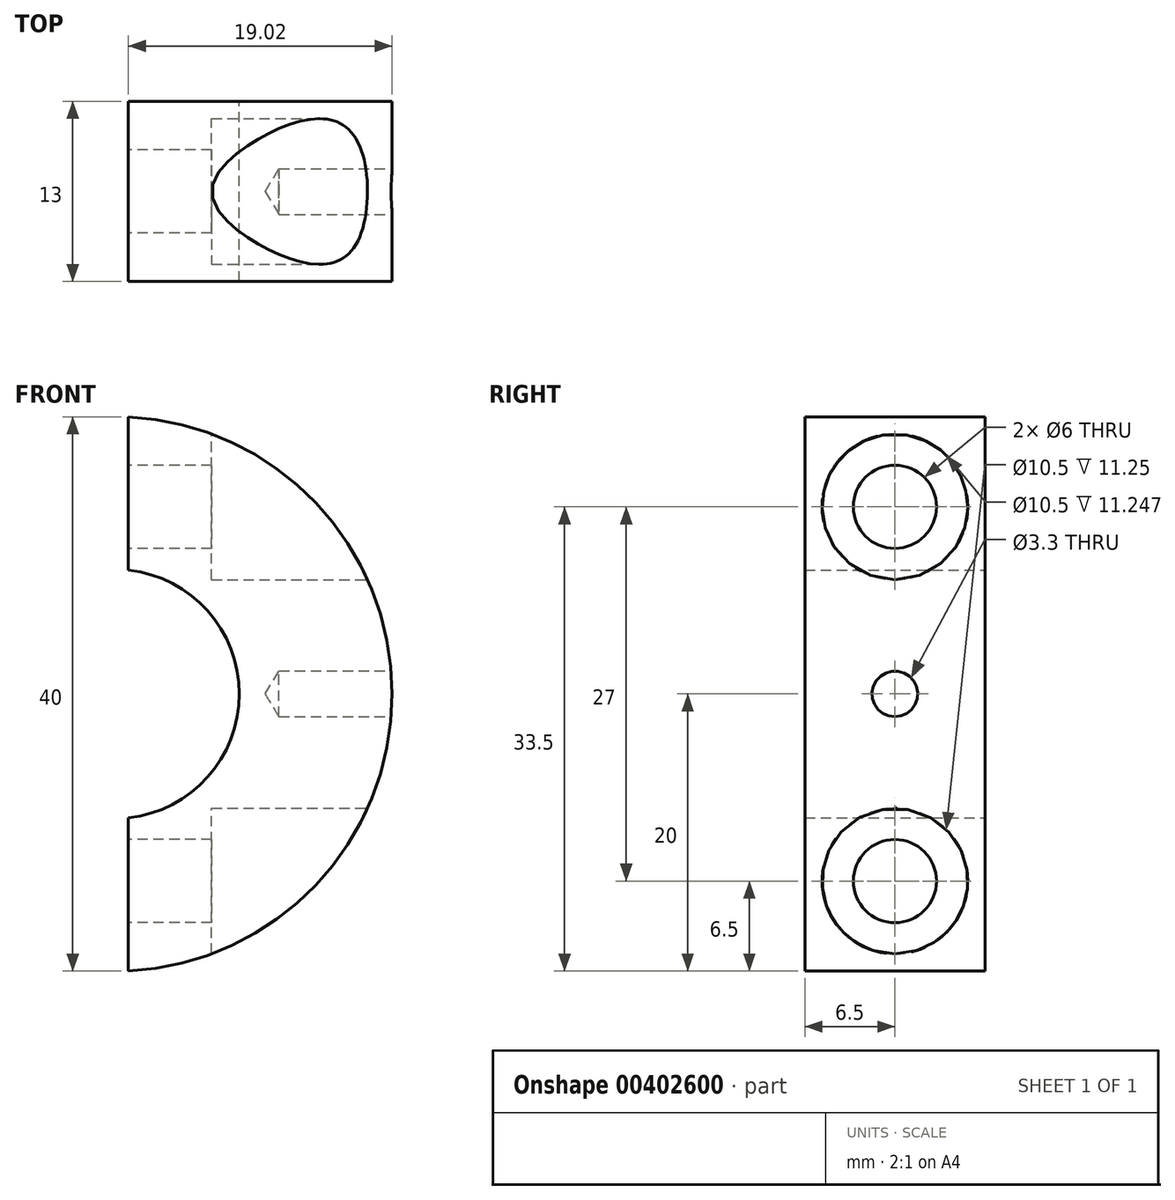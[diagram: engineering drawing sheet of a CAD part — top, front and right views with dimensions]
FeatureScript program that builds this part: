
annotation { "Feature Type Name" : "Feature", "Feature Type Description" : "" }
export const myFeature = defineFeature(function(context is Context, id is Id, definition is map)
    precondition{}
    {
        {
            var Q0;
            Q0=qCreatedBy(makeId("Front.planeOp"),FACE);
            var sketch = newSketch(context, id + "F0", { "sketchPlane" : qUnion([Q0])});
            skLineSegment(sketch, "E0", {"start": v(0, 0) * mm, "end": v(1, 0) * mm, "construction": true});
            skArc(sketch, "E1", {"start": v(1, -8.94) * mm, "mid": v(9, 0) * mm, "end": v(1, 8.94) * mm});
            skLineSegment(sketch, "E2", {"start": v(1, 0) * mm, "end": v(1, -8.94) * mm, "construction": true});
            skLineSegment(sketch, "E3", {"start": v(1, 0) * mm, "end": v(1, 8.94) * mm, "construction": true});
            skLineSegment(sketch, "E4", {"start": v(1, 8.94) * mm, "end": v(1, 20) * mm});
            skLineSegment(sketch, "E5", {"start": v(1, -8.94) * mm, "end": v(1, -20) * mm});
            skLineSegment(sketch, "E6", {"start": v(1, 13.5) * mm, "end": v(22.49, 13.5) * mm, "construction": true});
            skLineSegment(sketch, "E7", {"start": v(1, 16.5) * mm, "end": v(22.49, 16.5) * mm, "construction": true});
            skLineSegment(sketch, "E8", {"start": v(1, 10.5) * mm, "end": v(22.49, 10.5) * mm, "construction": true});
            skLineSegment(sketch, "E9", {"start": v(22.49, 16.5) * mm, "end": v(22.49, 13.5) * mm, "construction": true});
            skLineSegment(sketch, "E10", {"start": v(22.49, 13.5) * mm, "end": v(22.49, 10.5) * mm, "construction": true});
            skArc(sketch, "E11", {"start": v(1, -20) * mm, "mid": v(20.02, 0) * mm, "end": v(1, 20) * mm});
            skSolve(sketch);
        }
        {
            var Q0;
            Q0 = qSketchRegion(id + "F0", true);
            extrude(context, id + "F1", {"entities" : qUnion([Q0]), "depth" : 13 * mm});
        }
        {
            var Q0;
            Q0=makeQuery(id+"F1.opExtrude","SWEPT_FACE",FACE,{"disambiguationData":[OSD([sQuery(id+"F0.wireOp",EDGE,"E4")])]});
            var sketch = newSketch(context, id + "F2", { "sketchPlane" : qUnion([Q0])});
            skLineSegment(sketch, "E12", {"start": v(0, 0) * mm, "end": v(13.07, 0) * mm, "construction": true});
            skLineSegment(sketch, "E13", {"start": v(0, 13.5) * mm, "end": v(13, 13.5) * mm, "construction": true});
            skCircle(sketch, "E14", {"center": v(6.5, 13.5) * mm, "radius": 3 * mm});
            skLineSegment(sketch, "E15.MirrorCS", {"start": v(0, -13.5) * mm, "end": v(13, -13.5) * mm, "construction": true});
            skCircle(sketch, "E16.MirrorC", {"center": v(6.5, -13.5) * mm, "radius": 3 * mm});
            skSolve(sketch);
        }
        {
            var Q0;
            Q0 = qSketchRegion(id + "F2", true);
            extrude(context, id + "F3", {"entities" : qUnion([Q0]), "operationType" : NewBodyOperationType.REMOVE, "endBound" : BoundingType.THROUGH_ALL, "oppositeDirection" : true, "depth" : 25 * mm});
        }
        {
            var Q0;
            Q0=makeQuery(id+"F1.opExtrude","SWEPT_FACE",FACE,{"disambiguationData":[OSD([sQuery(id+"F0.wireOp",EDGE,"E5")])]});
            cPlane(context, id + "F4", {"entities" : qUnion([Q0]), "cplaneType" : CPlaneType.OFFSET, "offset" : 25 * mm, "oppositeDirection" : true, "width" : 150 * mm, "height" : 150 * mm});
        }
        {
            var Q0;
            Q0=qCreatedBy(id+"F4.planeOp",FACE);
            var sketch = newSketch(context, id + "F5", { "sketchPlane" : qUnion([Q0])});
            skCircle(sketch, "E17", {"center": v(6.5, -13.5) * mm, "radius": 5.25 * mm});
            skCircle(sketch, "E18", {"center": v(6.5, 13.5) * mm, "radius": 5.25 * mm});
            skSolve(sketch);
        }
        {
            var Q0;
            Q0 = qSketchRegion(id + "F5", true);
            extrude(context, id + "F6", {"entities" : qUnion([Q0]), "operationType" : NewBodyOperationType.REMOVE, "depth" : 19 * mm});
        }
        {
            var Q0;
            Q0=makeQuery(id+"F1.opExtrude","SWEPT_FACE",FACE,{"disambiguationData":[OSD([sQuery(id+"F0.wireOp",EDGE,"E4")])]});
            cPlane(context, id + "F7", {"entities" : qUnion([Q0]), "cplaneType" : CPlaneType.OFFSET, "offset" : 20 * mm, "oppositeDirection" : true, "width" : 150 * mm, "height" : 150 * mm});
        }
        {
            var Q0;
            Q0=qCreatedBy(id+"F7.planeOp",FACE);
            var sketch = newSketch(context, id + "F8", { "sketchPlane" : qUnion([Q0])});
            skLineSegment(sketch, "E19", {"start": v(13, 0) * mm, "end": v(0, 0) * mm, "construction": true});
            skCircle(sketch, "E20", {"center": v(6.5, 0) * mm, "radius": 2 * mm});
            skSolve(sketch);
        }
        {
            var Q0;
            Q0=sQuery(id+"F8.wireOp",VERTEX,"E20.center");
            var Q1;
            Q1=makeQuery(id+"F1.opExtrude","SWEPT_BODY",BODY,{"disambiguationData":[OSD([sQuery(id+"F0.wireOp",EDGE,"E1"),sQuery(id+"F0.wireOp",EDGE,"E4"),sQuery(id+"F0.wireOp",EDGE,"E5"),sQuery(id+"F0.wireOp",EDGE,"E11")])]});
            hole(context, id + "F9", {"style" : HoleStyle.SIMPLE, "endStyle" : HoleEndStyle.BLIND, "oppositeDirection" : true, "standardTappedOrClearance" : lookupTablePath({ "standard" : "ISO", "fit" : "Normal", "engagement" : "75%", "pitch" : "0.7 mm", "size" : "M4", "type" : "Tapped" }), "standardBlindInLast" : lookupTablePath({ "fit" : "Standard", "standard" : "ISO", "engagement" : "75%", "pitch" : "0.7 mm", "size" : "M4", "type" : "Tapped" }), "holeDiameter" : 3.3 * mm, "showTappedDepth" : true, "holeDepth" : 8.1 * mm, "tappedDepth" : 6 * mm, "tapClearance" : 3, "locations" : qUnion([Q0]), "scope" : qUnion([Q1]), "majorDiameter" : 4 * mm});
        }
    });
